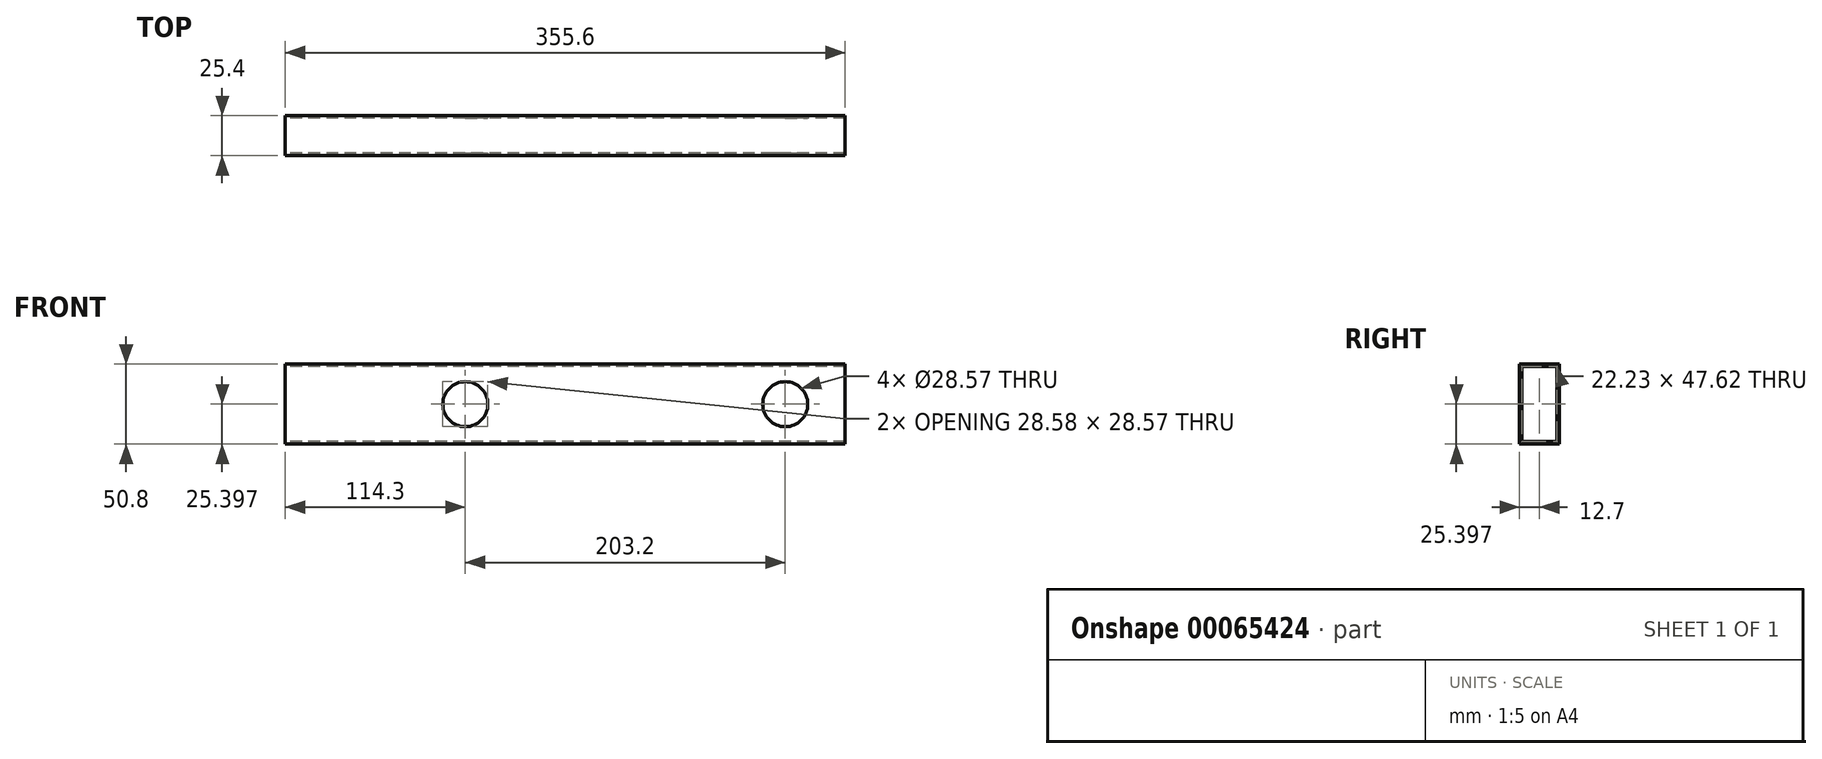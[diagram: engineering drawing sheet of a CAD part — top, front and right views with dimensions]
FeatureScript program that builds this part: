
annotation { "Feature Type Name" : "Feature", "Feature Type Description" : "" }
export const myFeature = defineFeature(function(context is Context, id is Id, definition is map)
    precondition{}
    {
        {
            var Q0;
            Q0=qCreatedBy(makeId("Right.planeOp"),FACE);
            var sketch = newSketch(context, id + "F0", { "sketchPlane" : qUnion([Q0])});
            skLineSegment(sketch, "E0.bottom", {"start": v(12.7, 23.37) * mm, "end": v(-12.7, 23.37) * mm});
            skLineSegment(sketch, "E0.top", {"start": v(12.7, -27.43) * mm, "end": v(-12.7, -27.43) * mm});
            skLineSegment(sketch, "E0.left", {"start": v(12.7, 23.37) * mm, "end": v(12.7, -27.43) * mm});
            skLineSegment(sketch, "E0.right", {"start": v(-12.7, 23.37) * mm, "end": v(-12.7, -27.43) * mm});
            skPoint(sketch, "E0.middle", {"position": v(0, -2.03) * mm});
            skLineSegment(sketch, "E1.bottom", {"start": v(11.11, 21.78) * mm, "end": v(-11.11, 21.78) * mm});
            skLineSegment(sketch, "E1.top", {"start": v(11.11, -25.85) * mm, "end": v(-11.11, -25.85) * mm});
            skLineSegment(sketch, "E1.left", {"start": v(11.11, 21.78) * mm, "end": v(11.11, -25.85) * mm});
            skLineSegment(sketch, "E1.right", {"start": v(-11.11, 21.78) * mm, "end": v(-11.11, -25.85) * mm});
            skSolve(sketch);
        }
        {
            var Q0;
            Q0=makeQuery(id+"F0.imprint","IMPRINT",FACE,{"disambiguationData":[TD([[makeQuery(id+"F0.imprint","IMPRINT",EDGE,{"derivedFrom":sQuery(id+"F0.wireOp",EDGE,"E0.bottom")}),1.0]])]});
            extrude(context, id + "F1", {"entities" : qUnion([Q0]), "depth" : 355.6 * mm});
        }
        {
            var Q0;
            Q0=makeQuery(id+"F1.opExtrude","SWEPT_FACE",FACE,{"disambiguationData":[OSD([sQuery(id+"F0.wireOp",EDGE,"E0.right")])]});
            var sketch = newSketch(context, id + "F2", { "sketchPlane" : qUnion([Q0])});
            skLineSegment(sketch, "E2", {"start": v(355.6, -2.03) * mm, "end": v(317.5, -2.03) * mm, "construction": true});
            skCircle(sketch, "E3", {"center": v(317.5, -2.03) * mm, "radius": 14.29 * mm});
            skLineSegment(sketch, "E4", {"start": v(317.5, -2.03) * mm, "end": v(114.3, -2.03) * mm, "construction": true});
            skCircle(sketch, "E5", {"center": v(114.3, -2.03) * mm, "radius": 14.29 * mm});
            skSolve(sketch);
        }
        {
            var Q0;
            Q0=makeQuery(id+"F2.imprint","IMPRINT",FACE,{"disambiguationData":[TD([[makeQuery(id+"F2.imprint","IMPRINT",EDGE,{"derivedFrom":sQuery(id+"F2.wireOp",EDGE,"E5")}),1.0]])]});
            var Q1;
            Q1=makeQuery(id+"F2.imprint","IMPRINT",FACE,{"disambiguationData":[TD([[makeQuery(id+"F2.imprint","IMPRINT",EDGE,{"derivedFrom":sQuery(id+"F2.wireOp",EDGE,"E3")}),1.0]])]});
            extrude(context, id + "F3", {"entities" : qUnion([Q0, Q1]), "operationType" : NewBodyOperationType.REMOVE, "oppositeDirection" : true, "depth" : 25.4 * mm});
        }
    });
